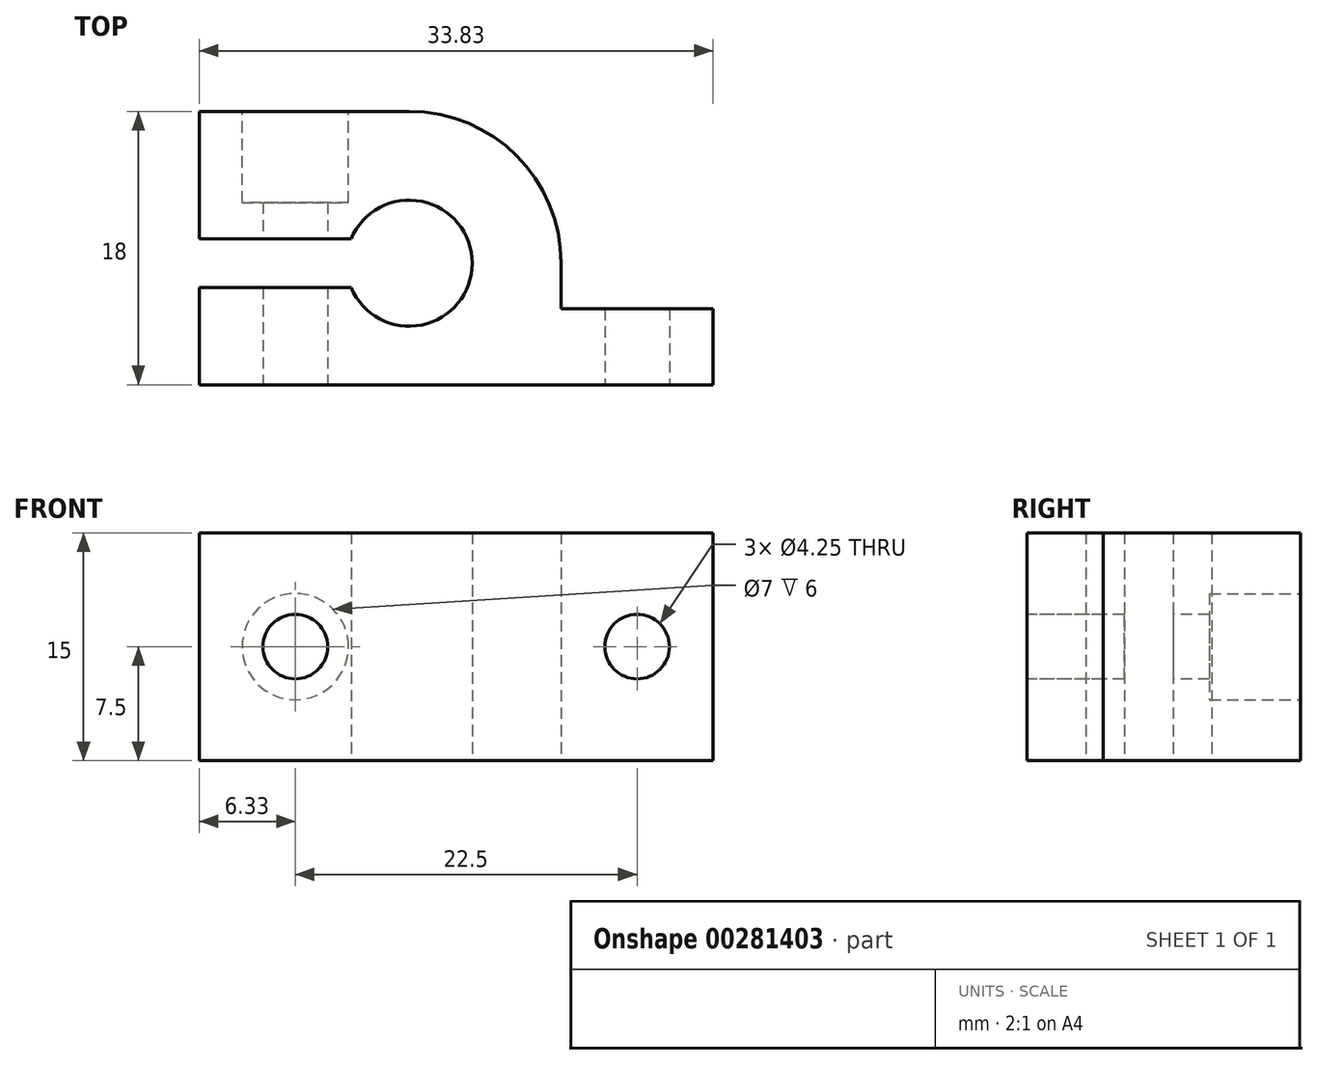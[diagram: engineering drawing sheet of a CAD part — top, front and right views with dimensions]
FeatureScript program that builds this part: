
annotation { "Feature Type Name" : "Feature", "Feature Type Description" : "" }
export const myFeature = defineFeature(function(context is Context, id is Id, definition is map)
    precondition{}
    {
        {
            var Q0;
            Q0=qCreatedBy(makeId("Top.planeOp"),FACE);
            var sketch = newSketch(context, id + "F0", { "sketchPlane" : qUnion([Q0])});
            skLineSegment(sketch, "E0", {"start": v(-13.83, 0) * mm, "end": v(20, 0) * mm});
            skLineSegment(sketch, "E1", {"start": v(20, 0) * mm, "end": v(20, 5) * mm});
            skLineSegment(sketch, "E2", {"start": v(20, 5) * mm, "end": v(10, 5) * mm});
            skLineSegment(sketch, "E3", {"start": v(0, 18) * mm, "end": v(-13.83, 18) * mm});
            skLineSegment(sketch, "E4", {"start": v(-13.83, 18) * mm, "end": v(-13.83, 9.6) * mm});
            skLineSegment(sketch, "E5", {"start": v(-13.83, 9.6) * mm, "end": v(-3.83, 9.6) * mm});
            skLineSegment(sketch, "E6", {"start": v(-3.83, 6.4) * mm, "end": v(-13.83, 6.4) * mm});
            skLineSegment(sketch, "E7", {"start": v(-13.83, 6.4) * mm, "end": v(-13.83, 0) * mm});
            skArc(sketch, "E8", {"start": v(-3.83, 6.4) * mm, "mid": v(4.15, 8) * mm, "end": v(-3.83, 9.6) * mm});
            skLineSegment(sketch, "E9", {"start": v(10, 5) * mm, "end": v(10, 8) * mm});
            skPoint(sketch, "E9.endSnap0", {"position": v(4.15, 8) * mm});
            skArc(sketch, "E10", {"start": v(10, 8) * mm, "mid": v(7.07, 15.07) * mm, "end": v(0, 18) * mm});
            skSolve(sketch);
        }
        {
            var Q0;
            Q0=qSketchRegion(id+"F0",true);
            extrude(context, id + "F1", {"entities" : qUnion([Q0]), "depth" : 15 * mm});
        }
        {
            var Q0;
            Q0=makeQuery(id+"F1.opExtrude","SWEPT_FACE",FACE,{"disambiguationData":[OSD([sQuery(id+"F0.wireOp",EDGE,"E0")])]});
            var sketch = newSketch(context, id + "F2", { "sketchPlane" : qUnion([Q0])});
            skCircle(sketch, "E11", {"center": v(-7.5, 7.5) * mm, "radius": 2.12 * mm});
            skCircle(sketch, "E12", {"center": v(15, 7.5) * mm, "radius": 2.12 * mm});
            skSolve(sketch);
        }
        {
            var Q0;
            Q0=qSketchRegion(id+"F2",true);
            extrude(context, id + "F3", {"entities" : qUnion([Q0]), "operationType" : NewBodyOperationType.REMOVE, "endBound" : BoundingType.THROUGH_ALL, "oppositeDirection" : true, "depth" : 20 * mm});
        }
        {
            var Q0;
            Q0=makeQuery(id+"F1.opExtrude","SWEPT_FACE",FACE,{"disambiguationData":[OSD([sQuery(id+"F0.wireOp",EDGE,"E3")])]});
            var sketch = newSketch(context, id + "F4", { "sketchPlane" : qUnion([Q0])});
            skCircle(sketch, "E13", {"center": v(7.5, 7.5) * mm, "radius": 3.5 * mm});
            skSolve(sketch);
        }
        {
            var Q0;
            Q0=qSketchRegion(id+"F4",true);
            extrude(context, id + "F5", {"entities" : qUnion([Q0]), "operationType" : NewBodyOperationType.REMOVE, "oppositeDirection" : true, "depth" : 6 * mm});
        }
    });
